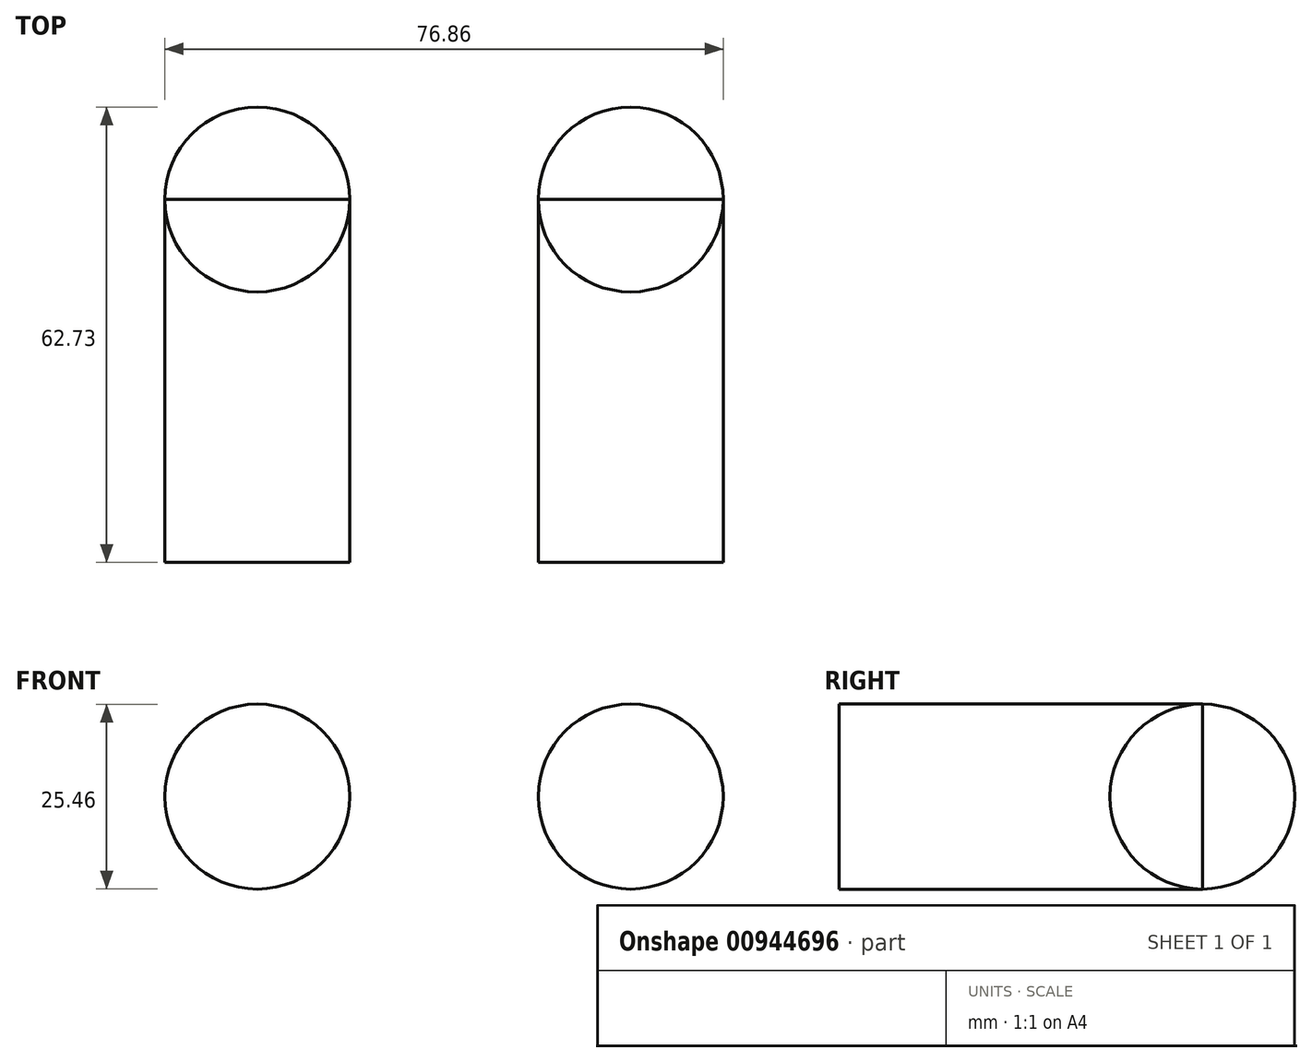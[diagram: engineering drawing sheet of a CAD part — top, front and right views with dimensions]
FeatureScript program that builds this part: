
annotation { "Feature Type Name" : "Feature", "Feature Type Description" : "" }
export const myFeature = defineFeature(function(context is Context, id is Id, definition is map)
    precondition{}
    {
        {
            var Q0;
            Q0=qCreatedBy(makeId("Front.planeOp"),FACE);
            var sketch = newSketch(context, id + "F0", { "sketchPlane" : qUnion([Q0])});
            skLineSegment(sketch, "E0", {"start": v(0, 0) * mm, "end": v(25.7, 0) * mm});
            skLineSegment(sketch, "E1.MirrorCS", {"start": v(0, 0) * mm, "end": v(-25.7, 0) * mm});
            skCircle(sketch, "E2", {"center": v(-25.7, 0) * mm, "radius": 12.73 * mm});
            skCircle(sketch, "E3.MirrorC", {"center": v(25.7, 0) * mm, "radius": 12.73 * mm});
            skLineSegment(sketch, "E4", {"start": v(25.7, 0) * mm, "end": v(38.43, 0) * mm});
            skLineSegment(sketch, "E5", {"start": v(-25.7, 0) * mm, "end": v(-38.43, 0) * mm});
            skSolve(sketch);
        }
        {
            var Q0;
            Q0 = qSketchRegion(id + "F0", true);
            extrude(context, id + "F1", {"entities" : qUnion([Q0]), "depth" : 50 * mm, "offsetDistance" : 25.4 * mm});
        }
        {
            var Q0;
            {var subQ0=sQuery(id+"F0.wireOp",EDGE,"E4");Q0=makeQuery(id+"F0.imprint","IMPRINT",FACE,{"disambiguationData":[TD([[makeQuery(id+"F0.imprint","IMPRINT",EDGE,{"derivedFrom":subQ0}),-1.0]])]});}
            var Q1;
            {var subQ0=sQuery(id+"F0.wireOp",EDGE,"E5");Q1=makeQuery(id+"F0.imprint","IMPRINT",FACE,{"disambiguationData":[TD([[makeQuery(id+"F0.imprint","IMPRINT",EDGE,{"derivedFrom":subQ0}),1.0]])]});}
            var Q2;
            Q2=sQuery(id+"F0.wireOp",EDGE,"E1.MirrorCS");
            revolve(context, id + "F2", {"surfaceOperationType" : NewSurfaceOperationType.NEW, "entities" : qUnion([Q0, Q1]), "axis" : qUnion([Q2]), "revolveType" : RevolveType.FULL});
        }
    });
